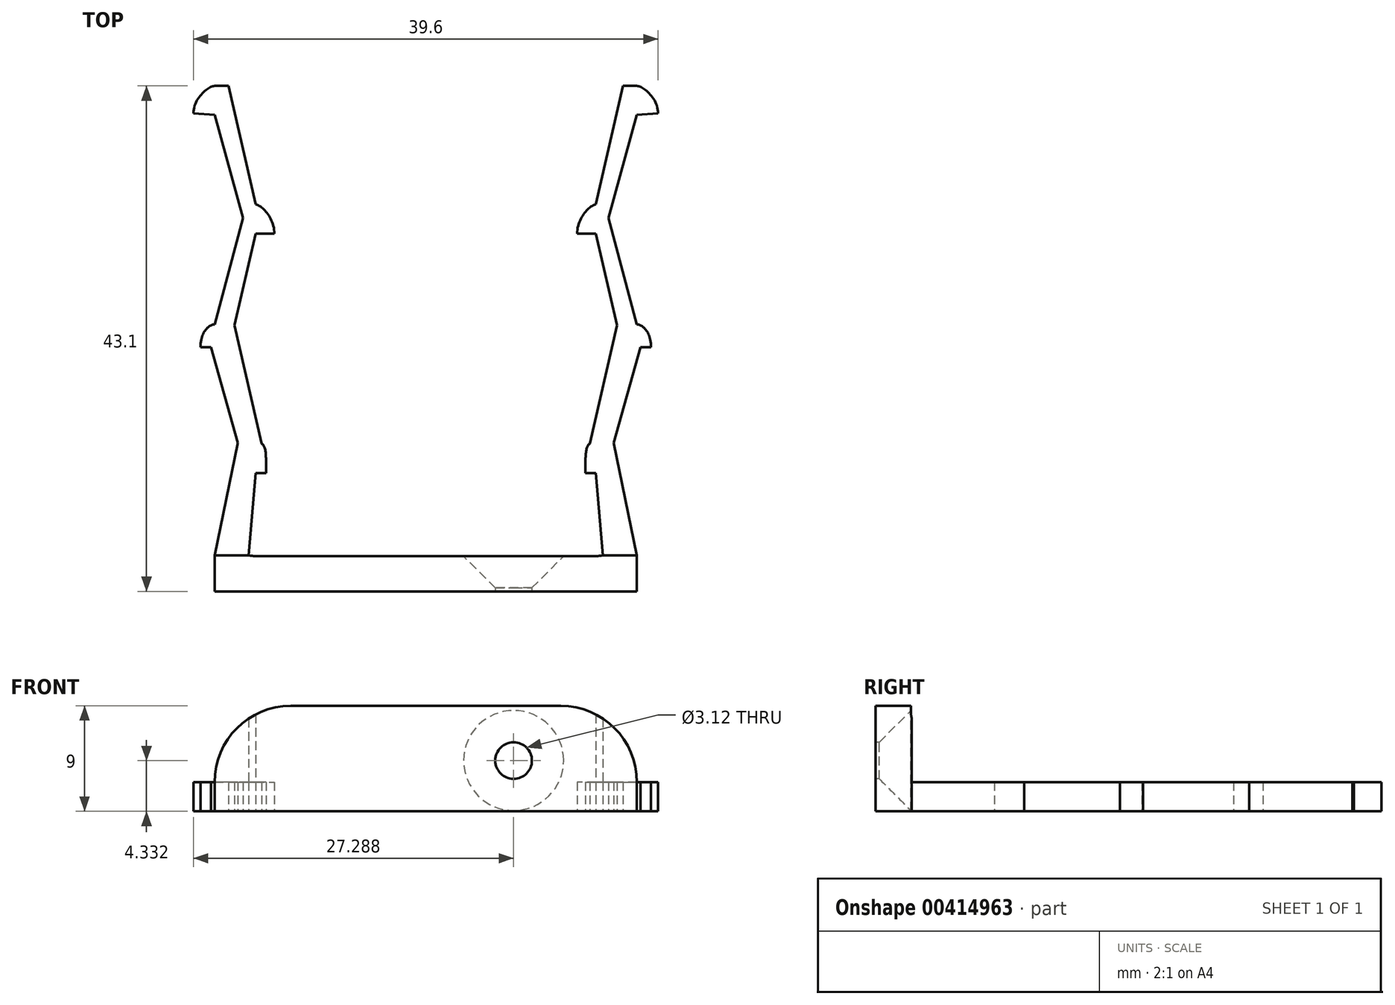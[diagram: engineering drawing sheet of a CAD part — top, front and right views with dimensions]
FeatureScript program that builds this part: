
annotation { "Feature Type Name" : "Feature", "Feature Type Description" : "" }
export const myFeature = defineFeature(function(context is Context, id is Id, definition is map)
    precondition{}
    {
        {
            var Q0;
            Q0=qCreatedBy(makeId("Top.planeOp"),FACE);
            var sketch = newSketch(context, id + "F0", { "sketchPlane" : qUnion([Q0])});
            skLineSegment(sketch, "E0.bottom", {"start": v(0, 0) * mm, "end": v(-14.5, 0) * mm});
            skLineSegment(sketch, "E0.top", {"start": v(0, 3) * mm, "end": v(-14.5, 3) * mm});
            skLineSegment(sketch, "E0.left", {"start": v(0, 0) * mm, "end": v(0, 3) * mm});
            skLineSegment(sketch, "E0.right", {"start": v(-14.5, 0) * mm, "end": v(-14.5, 3) * mm});
            skLineSegment(sketch, "E1.bottom", {"start": v(-14.5, 0) * mm, "end": v(-18, 0) * mm});
            skLineSegment(sketch, "E1.top", {"start": v(-14.5, 43.1) * mm, "end": v(-18, 43.1) * mm});
            skLineSegment(sketch, "E1.left", {"start": v(-14.5, 0) * mm, "end": v(-14.5, 43.1) * mm});
            skLineSegment(sketch, "E1.right", {"start": v(-18, 0) * mm, "end": v(-18, 43.1) * mm});
            skLineSegment(sketch, "E2", {"start": v(-14.5, 10.1) * mm, "end": v(-13.6, 10.1) * mm});
            skLineSegment(sketch, "E3", {"start": v(-14.5, 20.2) * mm, "end": v(-13.6, 20.2) * mm});
            skLineSegment(sketch, "E4", {"start": v(-14.5, 30.5) * mm, "end": v(-12.9, 30.5) * mm});
            skFitSpline(sketch, "E5", {"points": [v(-14.5, 22.7) * mm, v(-13.6, 20.2) * mm], "startDerivative": vector(1.54, -0.17) * mm, "endDerivative": vector(0.01, -4.03) * mm});
            skFitSpline(sketch, "E6", {"points": [v(-14.5, 33) * mm, v(-12.9, 30.5) * mm], "startDerivative": vector(1.69, -0.27) * mm, "endDerivative": vector(0.01, -4.03) * mm});
            skLineSegment(sketch, "E7", {"start": v(-14.5, 40.6) * mm, "end": v(-13.6, 40.6) * mm});
            skFitSpline(sketch, "E8", {"points": [v(-14.5, 43.1) * mm, v(-13.6, 40.6) * mm], "startDerivative": vector(1.54, -0.06) * mm, "endDerivative": vector(0.01, -4.03) * mm});
            skLineSegment(sketch, "E9.MirrorCS", {"start": v(14.5, 20.2) * mm, "end": v(13.6, 20.2) * mm});
            skFitSpline(sketch, "E10.MirrorCS", {"points": [v(14.5, 43.1) * mm, v(13.6, 40.6) * mm], "startDerivative": vector(-1.54, -0.06) * mm, "endDerivative": vector(-0.01, -4.03) * mm});
            skLineSegment(sketch, "E11.MirrorCS", {"start": v(14.5, 0) * mm, "end": v(18, 0) * mm});
            skLineSegment(sketch, "E12.MirrorCS", {"start": v(14.5, 10.1) * mm, "end": v(13.6, 10.1) * mm});
            skFitSpline(sketch, "E13.MirrorCS", {"points": [v(14.5, 22.7) * mm, v(13.6, 20.2) * mm], "startDerivative": vector(-1.54, -0.17) * mm, "endDerivative": vector(-0.01, -4.03) * mm});
            skLineSegment(sketch, "E14.MirrorCS", {"start": v(14.5, 30.5) * mm, "end": v(12.9, 30.5) * mm});
            skLineSegment(sketch, "E15.MirrorCS", {"start": v(14.5, 40.6) * mm, "end": v(13.6, 40.6) * mm});
            skFitSpline(sketch, "E16.MirrorCS", {"points": [v(14.5, 33) * mm, v(12.9, 30.5) * mm], "startDerivative": vector(-1.69, -0.27) * mm, "endDerivative": vector(-0.01, -4.03) * mm});
            skLineSegment(sketch, "E17.MirrorCS", {"start": v(14.5, 0) * mm, "end": v(14.5, 3) * mm});
            skLineSegment(sketch, "E18.MirrorCS", {"start": v(18, 0) * mm, "end": v(18, 43.1) * mm});
            skLineSegment(sketch, "E19.MirrorCS", {"start": v(14.5, 0) * mm, "end": v(14.5, 43.1) * mm});
            skLineSegment(sketch, "E20.MirrorCS", {"start": v(0, 3) * mm, "end": v(14.5, 3) * mm});
            skLineSegment(sketch, "E21.MirrorCS", {"start": v(0, 0) * mm, "end": v(14.5, 0) * mm});
            skLineSegment(sketch, "E22.MirrorCS", {"start": v(-18.3, 20.82) * mm, "end": v(-19.2, 20.82) * mm});
            skFitSpline(sketch, "E23.MirrorCS", {"points": [v(-18, 43.1) * mm, v(-19.8, 40.75) * mm], "startDerivative": vector(-1.54, -0.06) * mm, "endDerivative": vector(-0.01, -4.03) * mm});
            skLineSegment(sketch, "E24.MirrorCS", {"start": v(-18, 10.17) * mm, "end": v(-18.9, 10.17) * mm});
            skFitSpline(sketch, "E25.MirrorCS", {"points": [v(-18, 22.77) * mm, v(-19.2, 20.82) * mm], "startDerivative": vector(-1.54, -0.17) * mm, "endDerivative": vector(-0.01, -4.03) * mm});
            skLineSegment(sketch, "E26.MirrorCS", {"start": v(-18, 30.57) * mm, "end": v(-19.6, 30.57) * mm});
            skLineSegment(sketch, "E27.MirrorCS", {"start": v(-18, 40.63) * mm, "end": v(-19.8, 40.75) * mm});
            skFitSpline(sketch, "E28.MirrorCS", {"points": [v(-18, 33.07) * mm, v(-19.6, 30.57) * mm], "startDerivative": vector(-1.69, -0.27) * mm, "endDerivative": vector(-0.01, -4.03) * mm});
            skFitSpline(sketch, "E29.MirrorCS", {"points": [v(-18, 12.67) * mm, v(-18.9, 10.17) * mm], "startDerivative": vector(-1.24, 0.07) * mm, "endDerivative": vector(-0.01, -4.03) * mm});
            skLineSegment(sketch, "E30", {"start": v(14.5, 43.1) * mm, "end": v(18, 43.1) * mm});
            skFitSpline(sketch, "E31.MirrorCS", {"points": [v(18, 43.1) * mm, v(19.8, 40.75) * mm], "startDerivative": vector(1.54, -0.06) * mm, "endDerivative": vector(0.01, -4.03) * mm});
            skLineSegment(sketch, "E32.MirrorCS", {"start": v(18, 40.63) * mm, "end": v(19.8, 40.75) * mm});
            skFitSpline(sketch, "E33.MirrorCS", {"points": [v(18, 33.07) * mm, v(19.6, 30.57) * mm], "startDerivative": vector(1.69, -0.27) * mm, "endDerivative": vector(0.01, -4.03) * mm});
            skLineSegment(sketch, "E34.MirrorCS", {"start": v(18, 30.57) * mm, "end": v(19.6, 30.57) * mm});
            skFitSpline(sketch, "E35.MirrorCS", {"points": [v(18, 22.77) * mm, v(19.2, 20.82) * mm], "startDerivative": vector(1.54, -0.17) * mm, "endDerivative": vector(0.01, -4.03) * mm});
            skLineSegment(sketch, "E36.MirrorCS", {"start": v(18.3, 20.82) * mm, "end": v(19.2, 20.82) * mm});
            skFitSpline(sketch, "E37.MirrorCS", {"points": [v(18, 12.67) * mm, v(18.9, 10.17) * mm], "startDerivative": vector(1.24, 0.07) * mm, "endDerivative": vector(0.01, -4.03) * mm});
            skLineSegment(sketch, "E38.MirrorCS", {"start": v(18, 10.17) * mm, "end": v(18.9, 10.17) * mm});
            skLineSegment(sketch, "E39.bottom", {"start": v(-16.8, 43.1) * mm, "end": v(-15.7, 43.1) * mm});
            skLineSegment(sketch, "E40", {"start": v(-18, 3.06) * mm, "end": v(-16.01, 12.66) * mm});
            skLineSegment(sketch, "E41", {"start": v(-16.01, 12.66) * mm, "end": v(-18.3, 20.82) * mm});
            skLineSegment(sketch, "E42", {"start": v(-14, 12.6) * mm, "end": v(-16.3, 22.7) * mm});
            skLineSegment(sketch, "E43", {"start": v(-16.3, 22.7) * mm, "end": v(-14.5, 30.5) * mm});
            skLineSegment(sketch, "E44", {"start": v(-16.8, 43.1) * mm, "end": v(-14.5, 33) * mm});
            skLineSegment(sketch, "E45", {"start": v(-18, 40.63) * mm, "end": v(-15.57, 31.83) * mm});
            skLineSegment(sketch, "E46", {"start": v(-15.57, 31.83) * mm, "end": v(-18, 22.77) * mm});
            skLineSegment(sketch, "E47.MirrorCS", {"start": v(16.3, 22.7) * mm, "end": v(14.5, 30.5) * mm});
            skLineSegment(sketch, "E48.MirrorCS", {"start": v(15.57, 31.83) * mm, "end": v(18, 22.77) * mm});
            skLineSegment(sketch, "E49.MirrorCS", {"start": v(18, 40.63) * mm, "end": v(15.57, 31.83) * mm});
            skLineSegment(sketch, "E50.MirrorCS", {"start": v(16.8, 43.1) * mm, "end": v(14.5, 33) * mm});
            skLineSegment(sketch, "E51.MirrorCS", {"start": v(14, 12.6) * mm, "end": v(16.3, 22.7) * mm});
            skLineSegment(sketch, "E52.MirrorCS", {"start": v(16.01, 12.66) * mm, "end": v(18.3, 20.82) * mm});
            skLineSegment(sketch, "E53.MirrorCS", {"start": v(18, 3.06) * mm, "end": v(16.01, 12.66) * mm});
            skFitSpline(sketch, "E54", {"points": [v(-13.6, 10.1) * mm, v(-14, 12.6) * mm], "startDerivative": vector(-0.03, 4.13) * mm, "endDerivative": vector(-1.26, 0.5) * mm});
            skFitSpline(sketch, "E55.MirrorCS", {"points": [v(13.6, 10.1) * mm, v(14, 12.6) * mm], "startDerivative": vector(0.03, 4.13) * mm, "endDerivative": vector(1.26, 0.5) * mm});
            skLineSegment(sketch, "E56", {"start": v(-14.5, 10.1) * mm, "end": v(-15.1, 3.07) * mm});
            skLineSegment(sketch, "E57", {"start": v(-18, 3.06) * mm, "end": v(-15.1, 3.07) * mm});
            skLineSegment(sketch, "E58.MirrorCS", {"start": v(14.5, 10.1) * mm, "end": v(15.1, 3.07) * mm});
            skLineSegment(sketch, "E59.MirrorCS", {"start": v(18, 3.06) * mm, "end": v(15.1, 3.07) * mm});
            skLineSegment(sketch, "E60", {"start": v(-15.1, 3.07) * mm, "end": v(-14.5, 3) * mm});
            skLineSegment(sketch, "E61", {"start": v(14.5, 3) * mm, "end": v(15.1, 3.07) * mm});
            skSolve(sketch);
        }
        {
            var Q0;
            Q0=makeQuery(id+"F0.imprint","IMPRINT",FACE,{"disambiguationData":[TD([[makeQuery(id+"F0.imprint","IMPRINT",EDGE,{"derivedFrom":sQuery(id+"F0.wireOp",EDGE,"E40")}),-1.0]])]});
            var Q1;
            {var subQ0=sQuery(id+"F0.wireOp",EDGE,"E0.bottom");Q1=makeQuery(id+"F0.imprint","IMPRINT",FACE,{"disambiguationData":[TD([[makeQuery(id+"F0.imprint","IMPRINT",EDGE,{"derivedFrom":subQ0}),-1.0]])]});}
            var Q2;
            {var subQ2=sQuery(id+"F0.wireOp",EDGE,"E1.bottom");Q2=makeQuery(id+"F0.imprint","IMPRINT",FACE,{"disambiguationData":[TD([[makeQuery(id+"F0.imprint","IMPRINT",EDGE,{"derivedFrom":subQ2}),-1.0]])]});}
            var Q3;
            Q3=makeQuery(id+"F0.imprint","IMPRINT",FACE,{"disambiguationData":[TD([[makeQuery(id+"F0.imprint","IMPRINT",EDGE,{"derivedFrom":sQuery(id+"F0.wireOp",EDGE,"E0.left")}),-1.0]])]});
            var Q4;
            {var subQ2=sQuery(id+"F0.wireOp",EDGE,"E11.MirrorCS");Q4=makeQuery(id+"F0.imprint","IMPRINT",FACE,{"disambiguationData":[TD([[makeQuery(id+"F0.imprint","IMPRINT",EDGE,{"derivedFrom":subQ2}),1.0]])]});}
            var Q5;
            {var subQ5=sQuery(id+"F0.wireOp",EDGE,"E47.MirrorCS");Q5=makeQuery(id+"F0.imprint","IMPRINT",FACE,{"disambiguationData":[TD([[makeQuery(id+"F0.imprint","IMPRINT",EDGE,{"derivedFrom":subQ5}),-1.0]])]});}
            var Q6;
            {var subQ0=sQuery(id+"F0.wireOp",EDGE,"E12.MirrorCS");Q6=makeQuery(id+"F0.imprint","IMPRINT",FACE,{"disambiguationData":[TD([[makeQuery(id+"F0.imprint","IMPRINT",EDGE,{"derivedFrom":subQ0}),-1.0]])]});}
            var Q7;
            {var subQ0=sQuery(id+"F0.wireOp",EDGE,"E2");Q7=makeQuery(id+"F0.imprint","IMPRINT",FACE,{"disambiguationData":[TD([[makeQuery(id+"F0.imprint","IMPRINT",EDGE,{"derivedFrom":subQ0}),1.0]])]});}
            var Q8;
            {var subQ0=sQuery(id+"F0.wireOp",EDGE,"E35.MirrorCS");Q8=makeQuery(id+"F0.imprint","IMPRINT",FACE,{"disambiguationData":[TD([[makeQuery(id+"F0.imprint","IMPRINT",EDGE,{"derivedFrom":subQ0}),-1.0]])]});}
            var Q9;
            {var subQ0=sQuery(id+"F0.wireOp",EDGE,"E22.MirrorCS");Q9=makeQuery(id+"F0.imprint","IMPRINT",FACE,{"disambiguationData":[TD([[makeQuery(id+"F0.imprint","IMPRINT",EDGE,{"derivedFrom":subQ0}),-1.0]])]});}
            var Q10;
            {var subQ0=sQuery(id+"F0.wireOp",EDGE,"E14.MirrorCS");Q10=makeQuery(id+"F0.imprint","IMPRINT",FACE,{"disambiguationData":[TD([[makeQuery(id+"F0.imprint","IMPRINT",EDGE,{"derivedFrom":subQ0}),-1.0]])]});}
            var Q11;
            {var subQ0=sQuery(id+"F0.wireOp",EDGE,"E4");Q11=makeQuery(id+"F0.imprint","IMPRINT",FACE,{"disambiguationData":[TD([[makeQuery(id+"F0.imprint","IMPRINT",EDGE,{"derivedFrom":subQ0}),1.0]])]});}
            var Q12;
            {var subQ0=sQuery(id+"F0.wireOp",EDGE,"E23.MirrorCS");Q12=makeQuery(id+"F0.imprint","IMPRINT",FACE,{"disambiguationData":[TD([[makeQuery(id+"F0.imprint","IMPRINT",EDGE,{"derivedFrom":subQ0}),1.0]])]});}
            var Q13;
            {var subQ0=sQuery(id+"F0.wireOp",EDGE,"E31.MirrorCS");Q13=makeQuery(id+"F0.imprint","IMPRINT",FACE,{"disambiguationData":[TD([[makeQuery(id+"F0.imprint","IMPRINT",EDGE,{"derivedFrom":subQ0}),-1.0]])]});}
            extrude(context, id + "F1", {"entities" : qUnion([Q0, Q1, Q2, Q3, Q4, Q5, Q6, Q7, Q8, Q9, Q10, Q11, Q12, Q13]), "depth" : 2.5 * mm});
        }
        {
            var Q0;
            {var subQ2=sQuery(id+"F0.wireOp",EDGE,"E1.bottom");Q0=makeQuery(id+"F0.imprint","IMPRINT",FACE,{"disambiguationData":[TD([[makeQuery(id+"F0.imprint","IMPRINT",EDGE,{"derivedFrom":subQ2}),-1.0]])]});}
            var Q1;
            {var subQ0=sQuery(id+"F0.wireOp",EDGE,"E0.bottom");Q1=makeQuery(id+"F0.imprint","IMPRINT",FACE,{"disambiguationData":[TD([[makeQuery(id+"F0.imprint","IMPRINT",EDGE,{"derivedFrom":subQ0}),-1.0]])]});}
            var Q2;
            Q2=makeQuery(id+"F0.imprint","IMPRINT",FACE,{"disambiguationData":[TD([[makeQuery(id+"F0.imprint","IMPRINT",EDGE,{"derivedFrom":sQuery(id+"F0.wireOp",EDGE,"E0.left")}),-1.0]])]});
            var Q3;
            {var subQ2=sQuery(id+"F0.wireOp",EDGE,"E11.MirrorCS");Q3=makeQuery(id+"F0.imprint","IMPRINT",FACE,{"disambiguationData":[TD([[makeQuery(id+"F0.imprint","IMPRINT",EDGE,{"derivedFrom":subQ2}),1.0]])]});}
            extrude(context, id + "F2", {"entities" : qUnion([Q0, Q1, Q2, Q3]), "operationType" : NewBodyOperationType.ADD, "depth" : 9 * mm});
        }
        {
            var Q0;
            Q0=qCreatedBy(makeId("Front.planeOp"),FACE);
            var sketch = newSketch(context, id + "F3", { "sketchPlane" : qUnion([Q0])});
            skCircle(sketch, "E62", {"center": v(7.49, 4.33) * mm, "radius": 1.56 * mm});
            skCircle(sketch, "E63", {"center": v(0, 0) * mm, "radius": 2.66 * mm, "construction": true});
            skCircle(sketch, "E64.MirrorC", {"center": v(-7.49, 4.33) * mm, "radius": 1.56 * mm});
            skSolve(sketch);
        }
        {
            var Q0;
            Q0=makeQuery(id+"F3.imprint","IMPRINT",FACE,{"disambiguationData":[TD([[makeQuery(id+"F3.imprint","IMPRINT",EDGE,{"derivedFrom":sQuery(id+"F3.wireOp",EDGE,"E62")}),1.0]])]});
            var Q1;
            Q1=makeQuery(id+"F3.imprint","IMPRINT",FACE,{"disambiguationData":[TD([[makeQuery(id+"F3.imprint","IMPRINT",EDGE,{"derivedFrom":sQuery(id+"F3.wireOp",EDGE,"E64.MirrorC")}),-1.0]])]});
            extrude(context, id + "F4", {"entities" : qUnion([Q0, Q1]), "operationType" : NewBodyOperationType.REMOVE, "oppositeDirection" : true, "depth" : 25 * mm});
        }
        {
            var Q0;
            {var subQ0=sQuery(id+"F0.wireOp",EDGE,"E20.MirrorCS");var subQ1=sQuery(id+"F0.wireOp",EDGE,"E0.top");Q0=makeQuery(id+"F4.boolean.opBoolean","INTERSECT",EDGE,{"derivedFrom":[makeQuery(id+"F2.boolean.opBoolean","MERGE",FACE,{"derivedFrom":[makeQuery(id+"F1.opExtrude","SWEPT_FACE",FACE,{"disambiguationData":[OSD([subQ1,subQ0])]}),makeQuery(id+"F2.opExtrude","SWEPT_FACE",FACE,{"disambiguationData":[OSD([subQ1,subQ0])]})]}),makeQuery(id+"F4.opExtrude","SWEPT_FACE",FACE,{"disambiguationData":[OSD([sQuery(id+"F3.wireOp",EDGE,"E62")])]})]});}
            var Q1;
            {var subQ0=sQuery(id+"F0.wireOp",EDGE,"E20.MirrorCS");var subQ1=sQuery(id+"F0.wireOp",EDGE,"E0.top");Q1=makeQuery(id+"F4.boolean.opBoolean","INTERSECT",EDGE,{"derivedFrom":[makeQuery(id+"F2.boolean.opBoolean","MERGE",FACE,{"derivedFrom":[makeQuery(id+"F1.opExtrude","SWEPT_FACE",FACE,{"disambiguationData":[OSD([subQ1,subQ0])]}),makeQuery(id+"F2.opExtrude","SWEPT_FACE",FACE,{"disambiguationData":[OSD([subQ1,subQ0])]})]}),makeQuery(id+"F4.opExtrude","SWEPT_FACE",FACE,{"disambiguationData":[OSD([sQuery(id+"F3.wireOp",EDGE,"E64.MirrorC")])]})]});}
            chamfer(context, id + "F5", {"entities" : qUnion([Q0, Q1]), "width" : 2.7 * mm, "tangentPropagation" : true});
        }
        {
            var Q0;
            Q0=makeQuery(id+"F2.opExtrude","CAP_EDGE",EDGE,{"disambiguationData":[OSD([sQuery(id+"F0.wireOp",EDGE,"E1.right")])],"isStart":false});
            var Q1;
            Q1=makeQuery(id+"F2.opExtrude","CAP_EDGE",EDGE,{"disambiguationData":[OSD([sQuery(id+"F0.wireOp",EDGE,"E18.MirrorCS")])],"isStart":false});
            fillet(context, id + "F6", {"entities" : qUnion([Q0, Q1]), "radius" : 6.5 * mm, "tangentPropagation" : true, "allowEdgeOverflow" : false});
        }
    });
